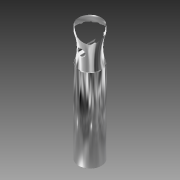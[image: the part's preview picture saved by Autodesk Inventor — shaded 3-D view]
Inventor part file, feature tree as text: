
AUTODESK INVENTOR PART (.ipt)
format: ipt  version: 2014 (Build 180170000, 170)  size: 155,648 bytes
history: native  units: mm (DEFAULTED — no unit token found)
features: sketch x1, revolve x1, extrude x1, chamfer x1
ambient origin geometry x8: Origin, YZ Plane, XZ Plane, XY Plane, X Axis, Y Axis, Z Axis, Center Point
bodies: Solid1 (feature_tree)
feature tree (4):
  sketch  "Sketch1"  dims[d0=3.96875mm d1=2.286mm d2=90.0deg d3=25.4mm d4=0.0mm d5=0.127mm d6=0.127mm d7=45.0deg]
  revolve  "Revolution1"  [1 undecoded]
  extrude  "Extrusion1"  TaperAngle=90.0deg  [1 undecoded]
  chamfer  "Chamfer1"  Distance=25.4mm
note: 2 required parameter values undecoded (feature->parameter linkage not recoverable at this tier; creation-order binding heuristic only, values carry confidence <= 0.55)